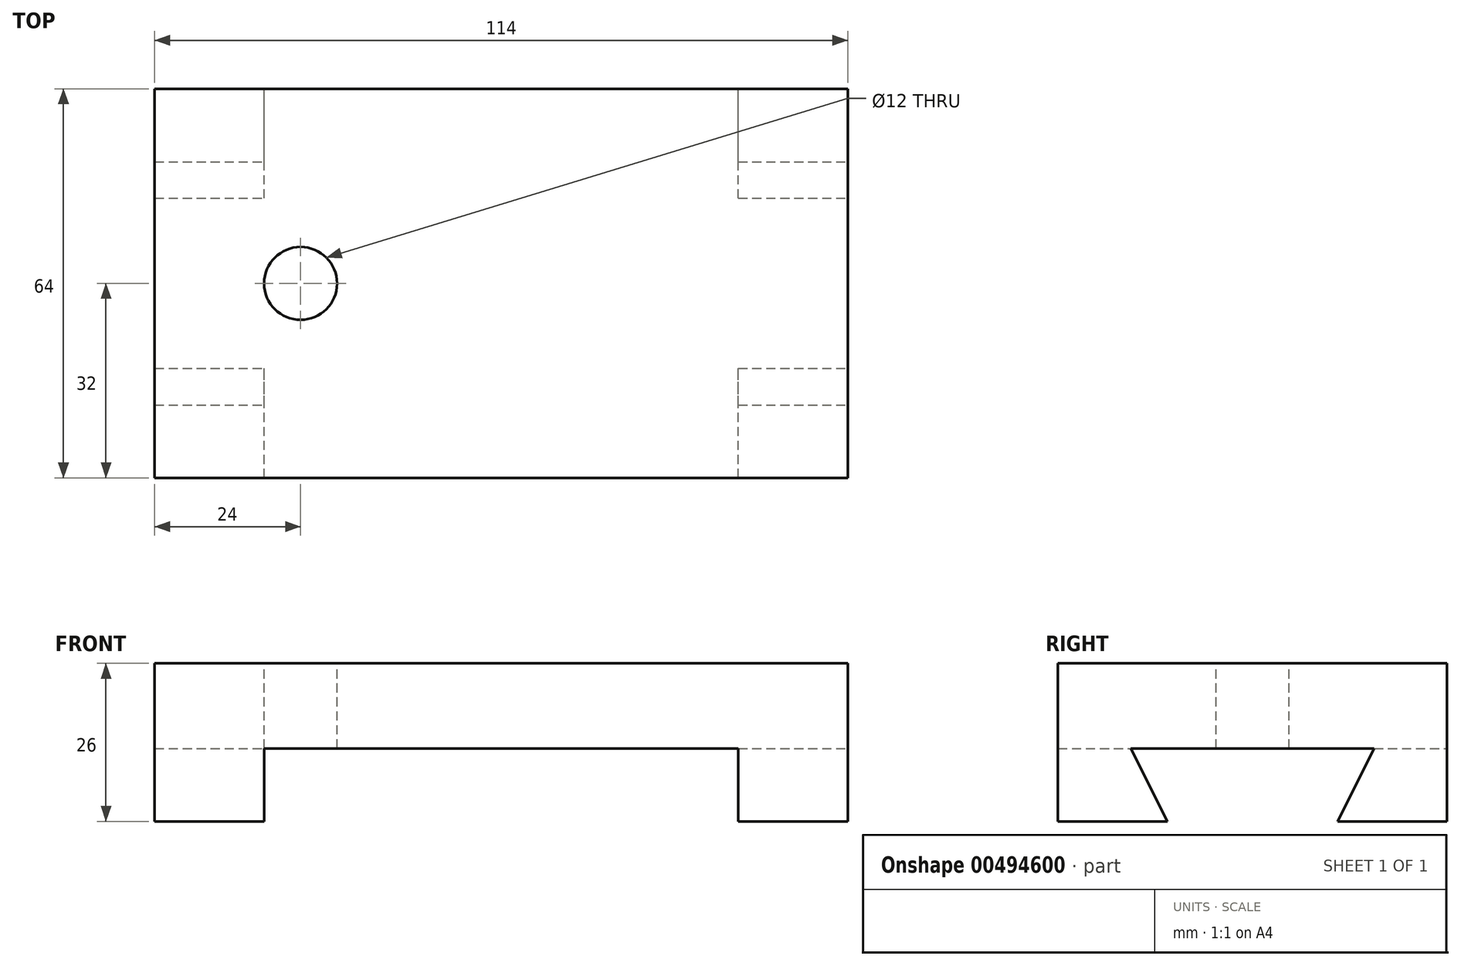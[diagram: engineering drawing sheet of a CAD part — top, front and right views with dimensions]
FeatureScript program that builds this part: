
annotation { "Feature Type Name" : "Feature", "Feature Type Description" : "" }
export const myFeature = defineFeature(function(context is Context, id is Id, definition is map)
    precondition{}
    {
        {
            var Q0;
            Q0=qCreatedBy(makeId("Front.planeOp"),FACE);
            var sketch = newSketch(context, id + "F0", { "sketchPlane" : qUnion([Q0])});
            skLineSegment(sketch, "E0", {"start": v(-58.4, 0) * mm, "end": v(-40.4, 0) * mm});
            skLineSegment(sketch, "E1", {"start": v(-58.4, 0) * mm, "end": v(-58.4, 26) * mm});
            skLineSegment(sketch, "E2", {"start": v(-40.4, 0) * mm, "end": v(-40.4, 12) * mm});
            skLineSegment(sketch, "E3", {"start": v(-58.4, 26) * mm, "end": v(55.6, 26) * mm});
            skLineSegment(sketch, "E4", {"start": v(55.6, 26) * mm, "end": v(55.6, 0) * mm});
            skLineSegment(sketch, "E5", {"start": v(55.6, 0) * mm, "end": v(37.6, 0) * mm});
            skLineSegment(sketch, "E6", {"start": v(37.6, 0) * mm, "end": v(37.6, 12) * mm});
            skLineSegment(sketch, "E7", {"start": v(-40.4, 12) * mm, "end": v(37.6, 12) * mm});
            skSolve(sketch);
        }
        {
            var Q0;
            Q0 = qSketchRegion(id + "F0", true);
            extrude(context, id + "F1", {"entities" : qUnion([Q0]), "endBound" : BoundingType.SYMMETRIC, "depth" : 64 * mm, "offsetDistance" : 25 * mm});
        }
        {
            var Q0;
            Q0=makeQuery(id+"F1.opExtrude","SWEPT_FACE",FACE,{"disambiguationData":[OSD([sQuery(id+"F0.wireOp",EDGE,"E3")])]});
            var sketch = newSketch(context, id + "F2", { "sketchPlane" : qUnion([Q0])});
            skCircle(sketch, "E8", {"center": v(-34.4, 0) * mm, "radius": 6 * mm});
            skSolve(sketch);
        }
        {
            var Q0;
            Q0 = qSketchRegion(id + "F2", true);
            extrude(context, id + "F3", {"entities" : qUnion([Q0]), "operationType" : NewBodyOperationType.REMOVE, "oppositeDirection" : true, "depth" : 25 * mm, "offsetDistance" : 25 * mm});
        }
        {
            var Q0;
            Q0=makeQuery(id+"F1.opExtrude","SWEPT_FACE",FACE,{"disambiguationData":[OSD([sQuery(id+"F0.wireOp",EDGE,"E4")])]});
            var sketch = newSketch(context, id + "F4", { "sketchPlane" : qUnion([Q0])});
            skLineSegment(sketch, "E9", {"start": v(-32, 26) * mm, "end": v(-20, 26) * mm});
            skLineSegment(sketch, "E10", {"start": v(32, 26) * mm, "end": v(20, 26) * mm});
            skLineSegment(sketch, "E11", {"start": v(-20, 26) * mm, "end": v(-20, 46) * mm});
            skLineSegment(sketch, "E12", {"start": v(-20, 46) * mm, "end": v(20, 46) * mm});
            skLineSegment(sketch, "E13", {"start": v(20, 46) * mm, "end": v(20, 26) * mm});
            skArc(sketch, "E14", {"start": v(20, 46) * mm, "mid": v(0, 66) * mm, "end": v(-20, 46) * mm});
            skCircle(sketch, "E15", {"center": v(0, 46) * mm, "radius": 11 * mm});
            skSolve(sketch);
        }
        {
            var Q0;
            {var subQ1=sQuery(id+"F4.wireOp",EDGE,"E9");Q0=makeQuery(id+"F4.imprint","IMPRINT",FACE,{"disambiguationData":[TD([[makeQuery(id+"F4.imprint","IMPRINT",EDGE,{"derivedFrom":subQ1}),-1.0]])]});}
            var sketch = newSketch(context, id + "F5", { "sketchPlane" : qUnion([Q0])});
            skLineSegment(sketch, "E16", {"start": v(0, 0) * mm, "end": v(-14, 0) * mm});
            skLineSegment(sketch, "E17", {"start": v(0, 0) * mm, "end": v(14, 0) * mm});
            skLineSegment(sketch, "E18", {"start": v(-20, 12) * mm, "end": v(0, 12) * mm});
            skLineSegment(sketch, "E19", {"start": v(0, 12) * mm, "end": v(20, 12) * mm});
            skLineSegment(sketch, "E20", {"start": v(-14, 0) * mm, "end": v(-20, 12) * mm});
            skLineSegment(sketch, "E21", {"start": v(20, 12) * mm, "end": v(14, 0) * mm});
            skSolve(sketch);
        }
        {
            var Q0;
            Q0 = qSketchRegion(id + "F5", true);
            extrude(context, id + "F6", {"entities" : qUnion([Q0]), "operationType" : NewBodyOperationType.REMOVE, "oppositeDirection" : true, "depth" : 1000 * mm, "offsetDistance" : 25 * mm});
        }
    });
